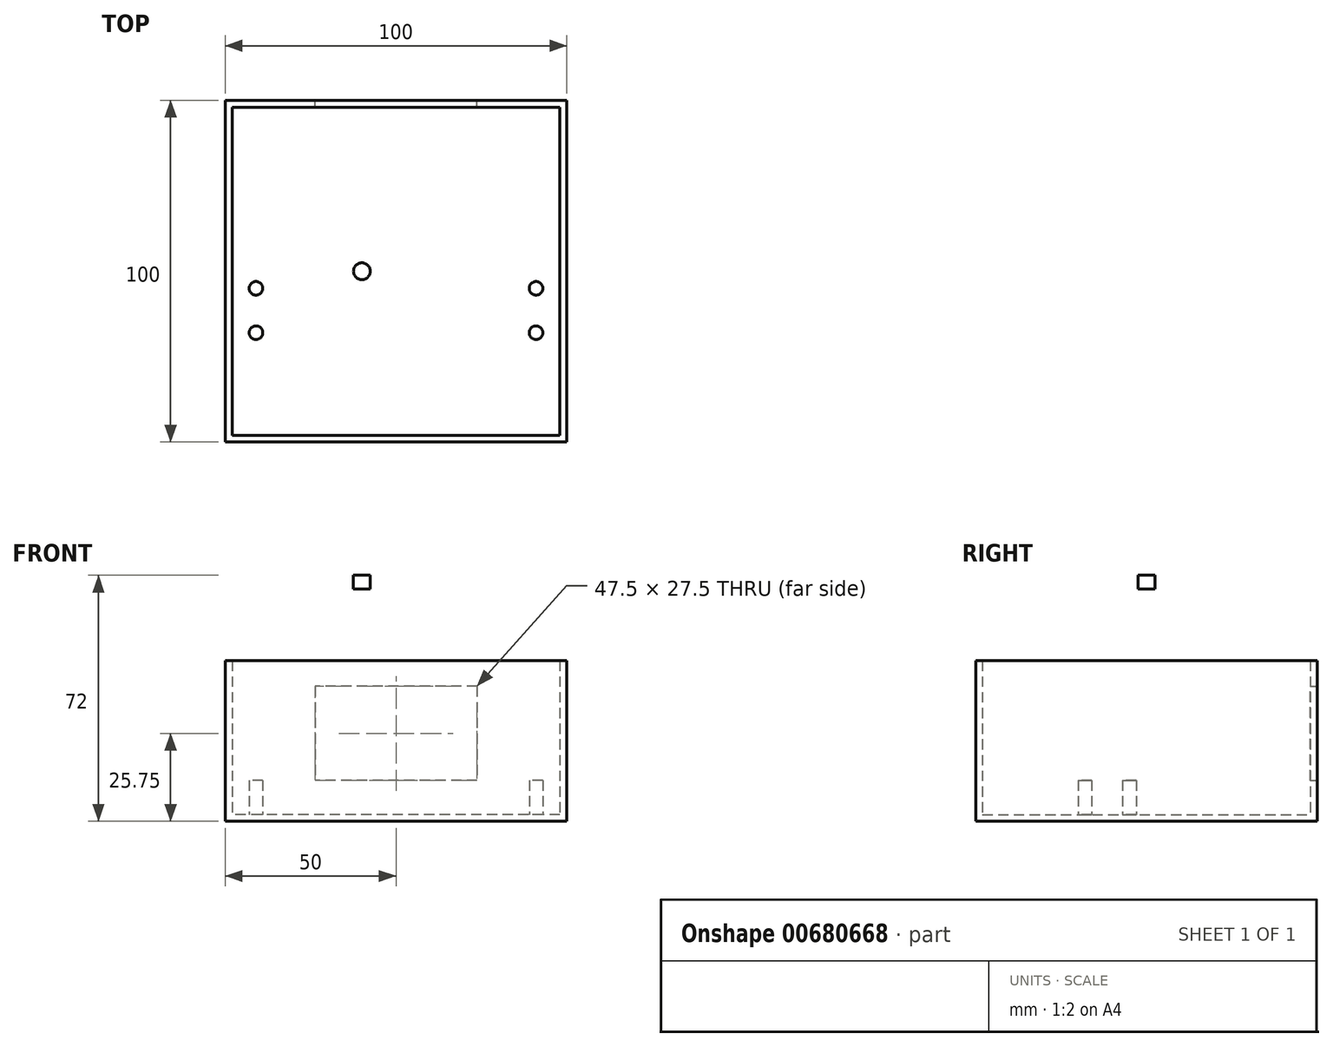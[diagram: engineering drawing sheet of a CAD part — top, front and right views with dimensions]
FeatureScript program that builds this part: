
annotation { "Feature Type Name" : "Feature", "Feature Type Description" : "" }
export const myFeature = defineFeature(function(context is Context, id is Id, definition is map)
    precondition{}
    {
        {
            var Q0;
            Q0=qCreatedBy(makeId("Top.planeOp"),FACE);
            var sketch = newSketch(context, id + "F0", { "sketchPlane" : qUnion([Q0])});
            skLineSegment(sketch, "E0.bottom", {"start": v(50, -50) * mm, "end": v(-50, -50) * mm});
            skLineSegment(sketch, "E0.top", {"start": v(50, 50) * mm, "end": v(-50, 50) * mm});
            skLineSegment(sketch, "E0.left", {"start": v(50, -50) * mm, "end": v(50, 50) * mm});
            skLineSegment(sketch, "E0.right", {"start": v(-50, -50) * mm, "end": v(-50, 50) * mm});
            skPoint(sketch, "E0.middle", {"position": v(0, 0) * mm});
            skSolve(sketch);
        }
        {
            var Q0;
            Q0 = qSketchRegion(id + "F0", true);
            extrude(context, id + "F1", {"entities" : qUnion([Q0]), "depth" : 70 * mm, "offsetDistance" : 25 * mm});
        }
        {
            var Q0;
            Q0=makeQuery(id+"F1.opExtrude","CAP_FACE",FACE,{"disambiguationData":[OSD([sQuery(id+"F0.wireOp",EDGE,"E0.bottom"),sQuery(id+"F0.wireOp",EDGE,"E0.top"),sQuery(id+"F0.wireOp",EDGE,"E0.left"),sQuery(id+"F0.wireOp",EDGE,"E0.right")])],"isStart":false});
            shell(context, id + "F2", {"entities" : qUnion([Q0]), "thickness" : 2 * mm});
        }
        {
            var Q0;
            Q0=makeQuery(id+"F2.opShell","OFFSET_FACE",FACE,{"disambiguationData":[OSD([sQuery(id+"F0.wireOp",EDGE,"E0.bottom"),sQuery(id+"F0.wireOp",EDGE,"E0.top"),sQuery(id+"F0.wireOp",EDGE,"E0.left"),sQuery(id+"F0.wireOp",EDGE,"E0.right")])]});
            var sketch = newSketch(context, id + "F3", { "sketchPlane" : qUnion([Q0])});
            skCircle(sketch, "E1", {"center": v(-41, -5) * mm, "radius": 2 * mm});
            skCircle(sketch, "E2", {"center": v(-41, -18) * mm, "radius": 2 * mm});
            skCircle(sketch, "E3.MirrorC", {"center": v(41, -5) * mm, "radius": 2 * mm});
            skCircle(sketch, "E4.MirrorC", {"center": v(41, -18) * mm, "radius": 2 * mm});
            skSolve(sketch);
        }
        {
            var Q0;
            Q0 = qSketchRegion(id + "F3", true);
            extrude(context, id + "F4", {"entities" : qUnion([Q0]), "operationType" : NewBodyOperationType.ADD, "depth" : 10 * mm, "offsetDistance" : 25 * mm});
        }
        {
            var Q0;
            Q0=makeQuery(id+"F1.opExtrude","SWEPT_FACE",FACE,{"disambiguationData":[OSD([sQuery(id+"F0.wireOp",EDGE,"E0.top")])]});
            var sketch = newSketch(context, id + "F5", { "sketchPlane" : qUnion([Q0])});
            skLineSegment(sketch, "E5.bottom", {"start": v(-23.75, 39.5) * mm, "end": v(23.75, 39.5) * mm});
            skLineSegment(sketch, "E5.top", {"start": v(-23.75, 12) * mm, "end": v(23.75, 12) * mm});
            skLineSegment(sketch, "E5.left", {"start": v(-23.75, 39.5) * mm, "end": v(-23.75, 12) * mm});
            skLineSegment(sketch, "E5.right", {"start": v(23.75, 39.5) * mm, "end": v(23.75, 12) * mm});
            skPoint(sketch, "E5.middle", {"position": v(0, 25.75) * mm});
            skSolve(sketch);
        }
        {
            var Q0;
            Q0 = qSketchRegion(id + "F5", true);
            extrude(context, id + "F6", {"entities" : qUnion([Q0]), "operationType" : NewBodyOperationType.REMOVE, "oppositeDirection" : true, "depth" : 25 * mm, "offsetDistance" : 25 * mm});
        }
        {
            var Q0;
            Q0=makeQuery(id+"F1.opExtrude","CAP_FACE",FACE,{"disambiguationData":[OSD([sQuery(id+"F0.wireOp",EDGE,"E0.bottom"),sQuery(id+"F0.wireOp",EDGE,"E0.top"),sQuery(id+"F0.wireOp",EDGE,"E0.left"),sQuery(id+"F0.wireOp",EDGE,"E0.right")])],"isStart":false});
            var sketch = newSketch(context, id + "F7", { "sketchPlane" : qUnion([Q0])});
            skLineSegment(sketch, "E6.0", {"start": v(48, -48) * mm, "end": v(48, 48) * mm, "construction": true});
            skLineSegment(sketch, "E6.1", {"start": v(48, 48) * mm, "end": v(-48, 48) * mm, "construction": true});
            skLineSegment(sketch, "E6.2", {"start": v(-48, -48) * mm, "end": v(-48, 48) * mm, "construction": true});
            skLineSegment(sketch, "E6.3", {"start": v(48, -48) * mm, "end": v(-48, -48) * mm, "construction": true});
            skLineSegment(sketch, "E7.0", {"start": v(50, -50) * mm, "end": v(-50, -50) * mm, "construction": true});
            skLineSegment(sketch, "E7.1", {"start": v(-50, -50) * mm, "end": v(-50, 50) * mm, "construction": true});
            skLineSegment(sketch, "E7.2", {"start": v(50, 50) * mm, "end": v(-50, 50) * mm, "construction": true});
            skLineSegment(sketch, "E7.3", {"start": v(50, -50) * mm, "end": v(50, 50) * mm, "construction": true});
            skLineSegment(sketch, "E8.bottom", {"start": v(47.75, -47.75) * mm, "end": v(-47.75, -47.75) * mm});
            skLineSegment(sketch, "E8.top", {"start": v(47.75, 47.75) * mm, "end": v(-47.75, 47.75) * mm});
            skLineSegment(sketch, "E8.left", {"start": v(47.75, -47.75) * mm, "end": v(47.75, 47.75) * mm});
            skLineSegment(sketch, "E8.right", {"start": v(-47.75, -47.75) * mm, "end": v(-47.75, 47.75) * mm});
            skPoint(sketch, "E8.middle", {"position": v(0, 0) * mm});
            skSolve(sketch);
        }
        {
            var Q0;
            Q0=makeQuery(id+"F7.imprint","IMPRINT",FACE,{"disambiguationData":[TD([[makeQuery(id+"F7.imprint","IMPRINT",EDGE,{"derivedFrom":sQuery(id+"F7.wireOp",EDGE,"E8.bottom")}),-1.0]])]});
            extrude(context, id + "F8", {"entities" : qUnion([Q0]), "oppositeDirection" : true, "depth" : 2 * mm, "offsetDistance" : 25 * mm});
        }
        {
            var Q0;
            Q0=makeQuery(id+"F8.opExtrude","CAP_FACE",FACE,{"disambiguationData":[OSD([sQuery(id+"F7.wireOp",EDGE,"E8.bottom"),sQuery(id+"F7.wireOp",EDGE,"E8.top"),sQuery(id+"F7.wireOp",EDGE,"E8.left"),sQuery(id+"F7.wireOp",EDGE,"E8.right")])],"isStart":true});
            var sketch = newSketch(context, id + "F9", { "sketchPlane" : qUnion([Q0])});
            skLineSegment(sketch, "E9.0", {"start": v(-50, -50) * mm, "end": v(-50, 50) * mm});
            skLineSegment(sketch, "E9.1", {"start": v(50, -50) * mm, "end": v(-50, -50) * mm});
            skLineSegment(sketch, "E9.2", {"start": v(50, 50) * mm, "end": v(-50, 50) * mm});
            skLineSegment(sketch, "E9.3", {"start": v(50, -50) * mm, "end": v(50, 50) * mm});
            skSolve(sketch);
        }
        {
            var Q0;
            Q0 = qSketchRegion(id + "F9", true);
            extrude(context, id + "F10", {"entities" : qUnion([Q0]), "operationType" : NewBodyOperationType.ADD, "depth" : 2 * mm, "offsetDistance" : 25 * mm});
        }
        {
            var Q0;
            Q0=makeQuery(id+"F10.opExtrude","CAP_FACE",FACE,{"disambiguationData":[OSD([sQuery(id+"F9.wireOp",EDGE,"E9.0"),sQuery(id+"F9.wireOp",EDGE,"E9.1"),sQuery(id+"F9.wireOp",EDGE,"E9.2"),sQuery(id+"F9.wireOp",EDGE,"E9.3")])],"isStart":false});
            var sketch = newSketch(context, id + "F11", { "sketchPlane" : qUnion([Q0])});
            skCircle(sketch, "E10", {"center": v(10, 0) * mm, "radius": 2.46 * mm});
            skCircle(sketch, "E11.MirrorC", {"center": v(-10, 0) * mm, "radius": 2.46 * mm});
            skSolve(sketch);
        }
        {
            var Q0;
            Q0=makeQuery(id+"F11.imprint","IMPRINT",FACE,{"disambiguationData":[TD([[makeQuery(id+"F11.imprint","IMPRINT",EDGE,{"derivedFrom":sQuery(id+"F11.wireOp",EDGE,"E10")}),1.0]])]});
            var Q1;
            Q1=makeQuery(id+"F11.imprint","IMPRINT",FACE,{"disambiguationData":[TD([[makeQuery(id+"F11.imprint","IMPRINT",EDGE,{"derivedFrom":sQuery(id+"F11.wireOp",EDGE,"E11.MirrorC")}),-1.0]])]});
            var Q2;
            Q2=sQuery(id+"F11.wireOp",EDGE,"E10");
            var Q3;
            Q3=sQuery(id+"F11.wireOp",EDGE,"E11.MirrorC");
            extrude(context, id + "F12", {"entities" : qUnion([Q0, Q1]), "operationType" : NewBodyOperationType.REMOVE, "surfaceEntities" : qUnion([Q2, Q3]), "oppositeDirection" : true, "depth" : 25 * mm, "offsetDistance" : 25 * mm});
        }
    });
